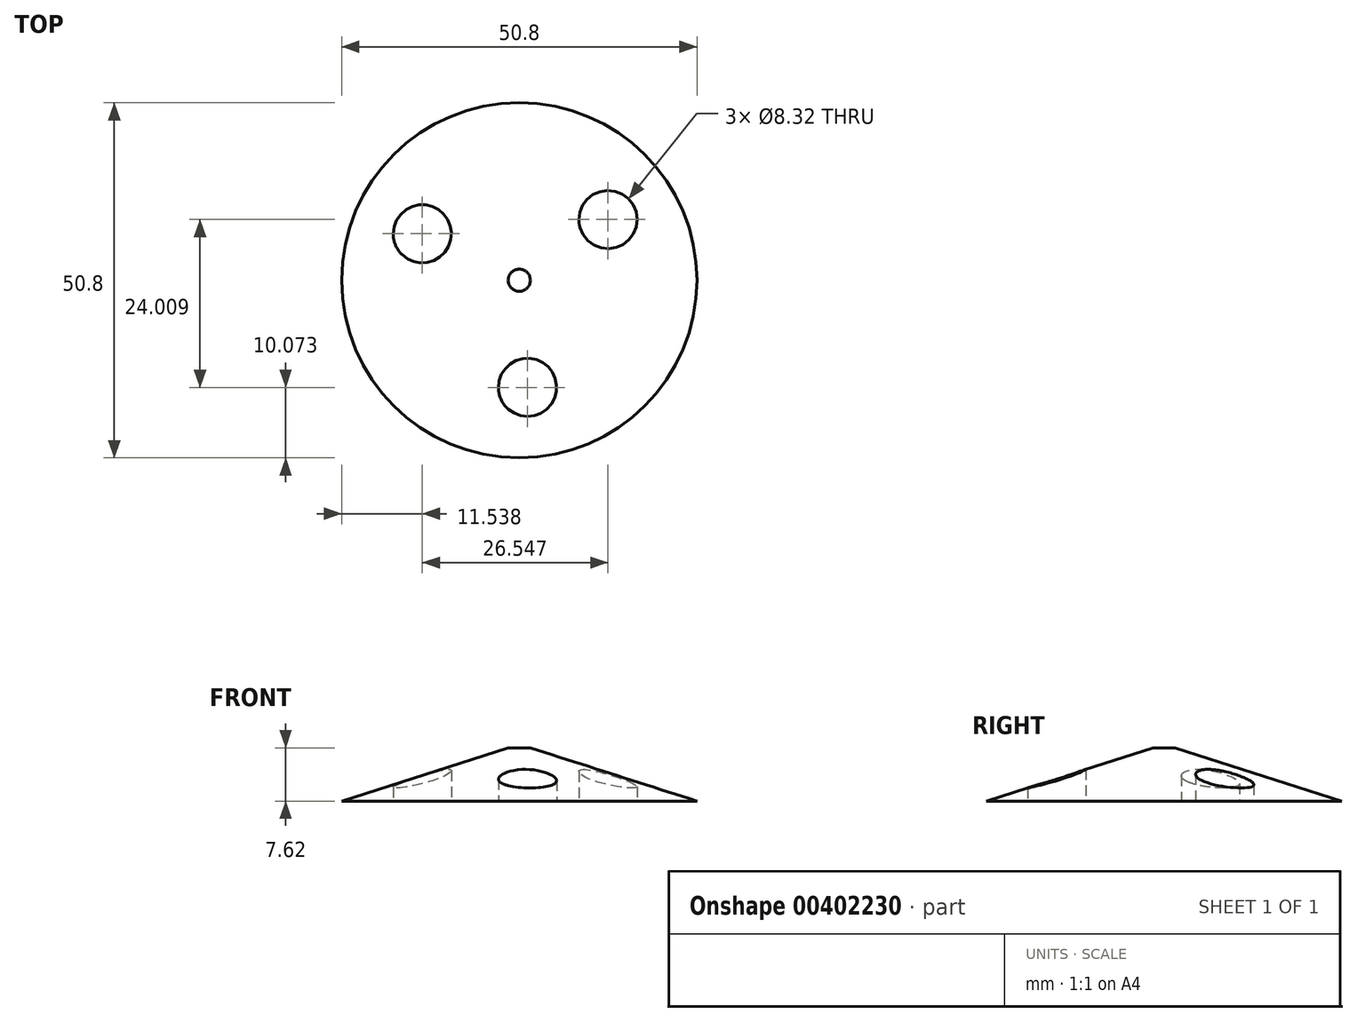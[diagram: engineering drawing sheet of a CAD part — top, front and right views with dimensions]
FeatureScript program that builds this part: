
annotation { "Feature Type Name" : "Feature", "Feature Type Description" : "" }
export const myFeature = defineFeature(function(context is Context, id is Id, definition is map)
    precondition{}
    {
        {
            var Q0;
            Q0=qCreatedBy(makeId("Top.planeOp"),FACE);
            cPlane(context, id + "F0", {"entities" : qUnion([Q0]), "cplaneType" : CPlaneType.OFFSET, "offset" : 7.62 * mm, "width" : 152.4 * mm, "height" : 152.4 * mm});
        }
        {
            var Q0;
            Q0=qCreatedBy(id+"F0.planeOp",FACE);
            var sketch = newSketch(context, id + "F1", { "sketchPlane" : qUnion([Q0])});
            skCircle(sketch, "E0", {"center": v(0, 0) * mm, "radius": 1.59 * mm});
            skSolve(sketch);
        }
        {
            var Q0;
            Q0=qCreatedBy(makeId("Top.planeOp"),FACE);
            var sketch = newSketch(context, id + "F2", { "sketchPlane" : qUnion([Q0])});
            skCircle(sketch, "E1", {"center": v(0, 0) * mm, "radius": 25.4 * mm});
            skSolve(sketch);
        }
        {
            var Q0;
            Q0=makeQuery(id+"F1.imprint","IMPRINT",FACE,{"disambiguationData":[TD([[makeQuery(id+"F1.imprint","IMPRINT",EDGE,{"derivedFrom":sQuery(id+"F1.wireOp",EDGE,"E0")}),1.0]])]});
            var Q1;
            Q1=makeQuery(id+"F2.imprint","IMPRINT",FACE,{"disambiguationData":[TD([[makeQuery(id+"F2.imprint","IMPRINT",EDGE,{"derivedFrom":sQuery(id+"F2.wireOp",EDGE,"E1")}),1.0]])]});
            loft(context, id + "F3", {"sheetProfilesArray" : [{ "sheetProfileEntities" : qUnion([Q0]) }, { "sheetProfileEntities" : qUnion([Q1]) }]});
        }
        {
            var Q0;
            Q0=makeQuery(id+"F3.opLoft","CAP_FACE",FACE,{"disambiguationData":[OSD([makeQuery(id+"F2.imprint","IMPRINT",FACE,{"disambiguationData":[TD([[makeQuery(id+"F2.imprint","IMPRINT",EDGE,{"derivedFrom":sQuery(id+"F2.wireOp",EDGE,"E1")}),1.0]])]})])],"isStart":true});
            var sketch = newSketch(context, id + "F4", { "sketchPlane" : qUnion([Q0])});
            skCircle(sketch, "E2", {"center": v(-13.86, -6.65) * mm, "radius": 4.16 * mm});
            skCircle(sketch, "E3.1.0", {"center": v(12.69, -8.68) * mm, "radius": 4.16 * mm});
            skCircle(sketch, "E3.2.0", {"center": v(1.18, 15.33) * mm, "radius": 4.16 * mm});
            skPoint(sketch, "E3.center", {"position": v(0, 0) * mm});
            skSolve(sketch);
        }
        {
            var Q0;
            Q0=makeQuery(id+"F4.imprint","IMPRINT",FACE,{"disambiguationData":[TD([[makeQuery(id+"F4.imprint","IMPRINT",EDGE,{"derivedFrom":sQuery(id+"F4.wireOp",EDGE,"E2")}),1.0]])]});
            var Q1;
            Q1=makeQuery(id+"F4.imprint","IMPRINT",FACE,{"disambiguationData":[TD([[makeQuery(id+"F4.imprint","IMPRINT",EDGE,{"derivedFrom":sQuery(id+"F4.wireOp",EDGE,"E3.2.0")}),1.0]])]});
            var Q2;
            Q2=makeQuery(id+"F4.imprint","IMPRINT",FACE,{"disambiguationData":[TD([[makeQuery(id+"F4.imprint","IMPRINT",EDGE,{"derivedFrom":sQuery(id+"F4.wireOp",EDGE,"E3.1.0")}),1.0]])]});
            extrude(context, id + "F5", {"entities" : qUnion([Q0, Q1, Q2]), "operationType" : NewBodyOperationType.REMOVE, "oppositeDirection" : true, "depth" : 25.4 * mm});
        }
    });
